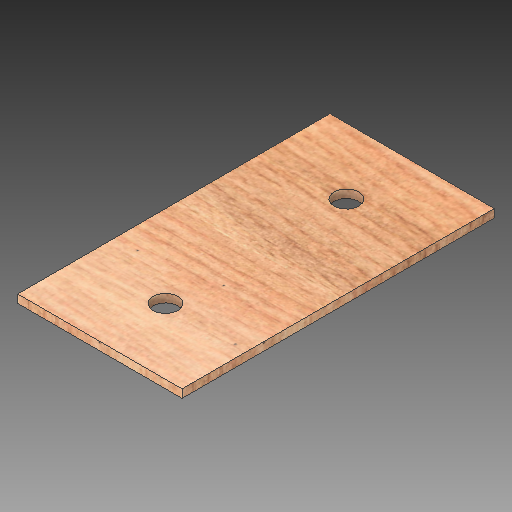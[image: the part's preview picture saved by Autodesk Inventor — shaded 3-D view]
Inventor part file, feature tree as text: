
AUTODESK INVENTOR PART (.ipt)
format: ipt  version: 2017 (Build 210142000, 142)  size: 245,248 bytes
history: native  units: in
note: dims shown in document units (in); Inventor stores cm internally (conversion verified against a paired STEP export)
features: extrude x2, sketch x2
ambient origin geometry x8: Origin, YZ Plane, XZ Plane, XY Plane, X Axis, Y Axis, Z Axis, Center Point
bodies: Solid1 (feature_tree)
feature tree (4):
  extrude  "Extrusion1"  Depth=9.5in
  extrude  "Extrusion2"  Depth=0.25in
  sketch  "Sketch1"  dims[d0=5.0in d1=9.5in]
  sketch  "Sketch2"  dims[d2=0.25in d3=0.0in d4=0.75in d5=0.75in d6=2.0in d7=2.0in d8=2.5in d9=2.5in d10=1.0in d11=0.0in]
